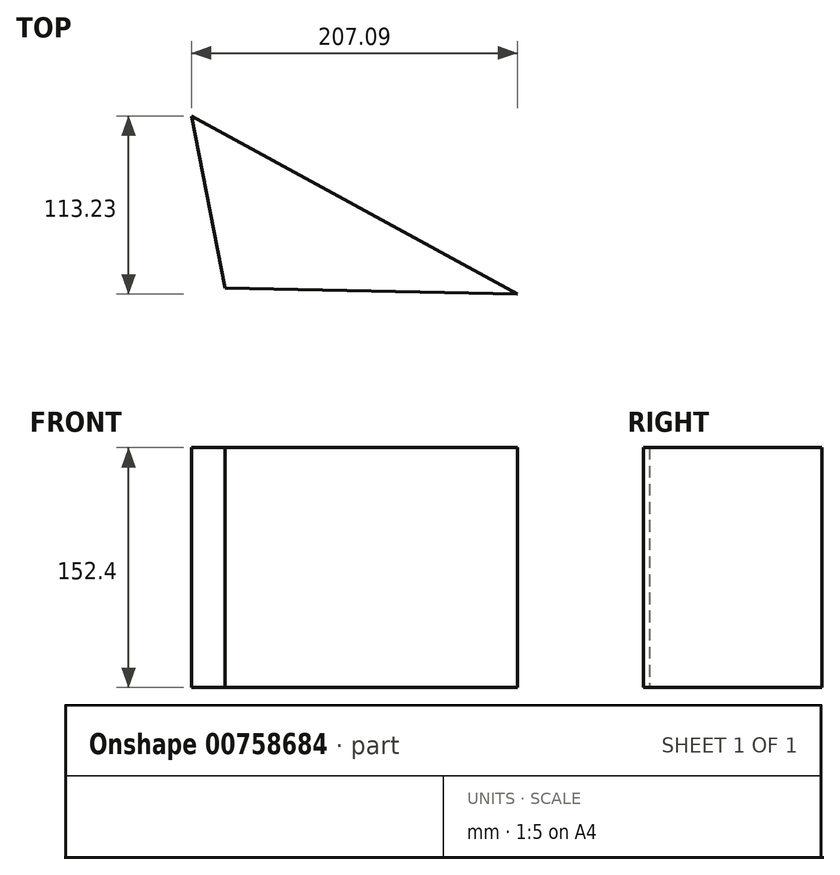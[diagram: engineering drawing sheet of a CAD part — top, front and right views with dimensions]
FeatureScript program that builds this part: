
annotation { "Feature Type Name" : "Feature", "Feature Type Description" : "" }
export const myFeature = defineFeature(function(context is Context, id is Id, definition is map)
    precondition{}
    {
        {
            var Q0;
            Q0=qCreatedBy(makeId("Top.planeOp"),FACE);
            var sketch = newSketch(context, id + "F0", { "sketchPlane" : qUnion([Q0])});
            skLineSegment(sketch, "E0", {"start": v(-21.3, 113.23) * mm, "end": v(-0.04, 3.8) * mm});
            skLineSegment(sketch, "E1", {"start": v(-0.04, 3.8) * mm, "end": v(185.8, 0) * mm});
            skLineSegment(sketch, "E2", {"start": v(185.8, 0) * mm, "end": v(-21.3, 113.23) * mm});
            skSolve(sketch);
        }
        {
            var Q0;
            Q0 = qSketchRegion(id + "F0", true);
            var Q1;
            Q1=makeQuery(id+"F0.imprint","IMPRINT",FACE,{"disambiguationData":[TD([[makeQuery(id+"F0.imprint","IMPRINT",EDGE,{"derivedFrom":sQuery(id+"F0.wireOp",EDGE,"E0")}),1.0]])]});
            extrude(context, id + "F1", {"entities" : qUnion([Q0, Q1]), "depth" : 152.4 * mm, "offsetDistance" : 25.4 * mm});
        }
    });
